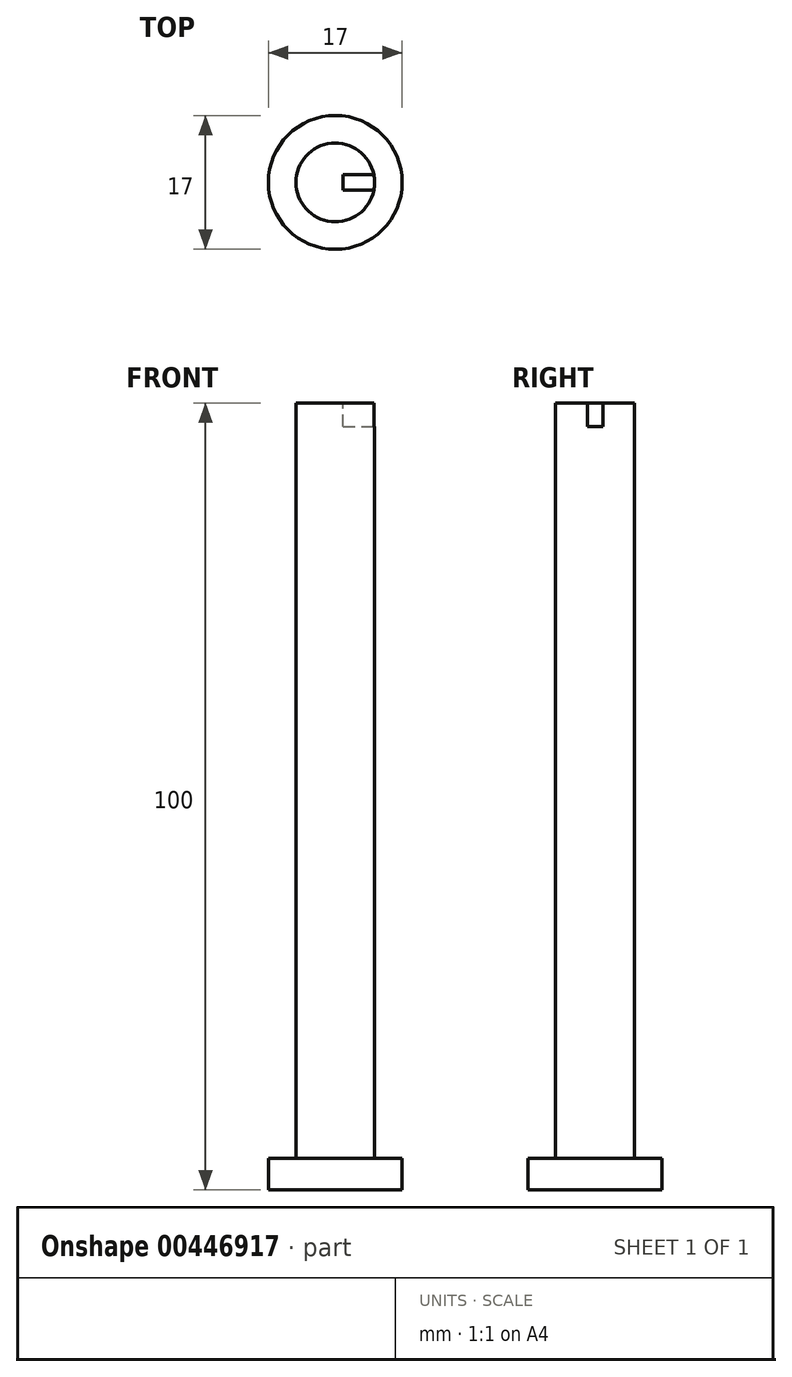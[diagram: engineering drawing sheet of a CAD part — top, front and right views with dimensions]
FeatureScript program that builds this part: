
annotation { "Feature Type Name" : "Feature", "Feature Type Description" : "" }
export const myFeature = defineFeature(function(context is Context, id is Id, definition is map)
    precondition{}
    {
        {
            var Q0;
            Q0=qCreatedBy(makeId("Top.planeOp"),FACE);
            var sketch = newSketch(context, id + "F0", { "sketchPlane" : qUnion([Q0])});
            skCircle(sketch, "E0", {"center": v(0, 0) * mm, "radius": 8.5 * mm});
            skSolve(sketch);
        }
        {
            var Q0;
            Q0=qSketchRegion(id+"F0",true);
            extrude(context, id + "F1", {"entities" : qUnion([Q0]), "depth" : 4 * mm});
        }
        {
            var Q0;
            Q0=qCreatedBy(makeId("Top.planeOp"),FACE);
            var sketch = newSketch(context, id + "F2", { "sketchPlane" : qUnion([Q0])});
            skCircle(sketch, "E1", {"center": v(0, 0) * mm, "radius": 5 * mm});
            skSolve(sketch);
        }
        {
            var Q0;
            Q0=qSketchRegion(id+"F2",true);
            extrude(context, id + "F3", {"entities" : qUnion([Q0]), "operationType" : NewBodyOperationType.ADD, "depth" : 100 * mm});
        }
        {
            var Q0;
            Q0=makeQuery(id+"F3.opExtrude","CAP_FACE",FACE,{"disambiguationData":[OSD([sQuery(id+"F2.wireOp",EDGE,"E1")])],"isStart":false});
            var sketch = newSketch(context, id + "F4", { "sketchPlane" : qUnion([Q0])});
            skLineSegment(sketch, "E2.bottom", {"start": v(1, 1) * mm, "end": v(5, 1) * mm});
            skLineSegment(sketch, "E2.top", {"start": v(1, -1) * mm, "end": v(5, -1) * mm});
            skLineSegment(sketch, "E2.left", {"start": v(1, 1) * mm, "end": v(1, -1) * mm});
            skLineSegment(sketch, "E2.right", {"start": v(5, 1) * mm, "end": v(5, -1) * mm});
            skSolve(sketch);
        }
        {
            var Q0;
            {var subQ4=sQuery(id+"F4.wireOp",EDGE,"E2.left");Q0=makeQuery(id+"F4.imprint","IMPRINT",FACE,{"disambiguationData":[TD([[makeQuery(id+"F4.imprint","IMPRINT",EDGE,{"derivedFrom":subQ4}),1.0]])]});}
            extrude(context, id + "F5", {"entities" : qUnion([Q0]), "operationType" : NewBodyOperationType.REMOVE, "oppositeDirection" : true, "depth" : 3 * mm});
        }
    });
